# Revit family: colum
name_source: partatom
category: Tragwerksstützen
revit_build: Autodesk Revit 2018 (Build: 20190510_1515(x64)
units: mm (PartAtom-declared; Revit-internal decimal feet)

## family parameters
Beim Laden mit Abzugskörper schneiden = Nein
Gemeinsam genutzt = Nein
Immer als Geometrie exportieren = Nein
In verdeckten Ansichten anzeigen = Von anderen Elementen verdeckte Kanten
Material für Modellverhalten = Fertigbeton
Querschnittsform = Nicht definiert
Schnittebene der Familie für Draufsichten verwenden = Ja
Trägerkürzung in Plan = Nach Begrenzungsrahmen

## types (5) — shared parameters
Kopfhoehe = 300 mm

## per-type parameters (varying)
| type | Durchmesser | KB_ | KT_ | Kopfbreite | Kopftiefe | Radius |
| D=20 | 200 mm  [stored 0.656168 ft] | 100 mm  [stored 0.328084 ft] | 100 mm  [stored 0.328084 ft] | 200 mm  [stored 0.656168 ft] | 200 mm  [stored 0.656168 ft] | 100 mm  [stored 0.328084 ft] |
| D=50 | 500 mm | 250 mm | 250 mm | 500 mm | 500 mm | 250 mm |
| D=40 | 400 mm  [stored 1.31234 ft] | 200 mm  [stored 0.656168 ft] | 200 mm  [stored 0.656168 ft] | 400 mm  [stored 1.31234 ft] | 400 mm  [stored 1.31234 ft] | 200 mm  [stored 0.656168 ft] |
| D=60 | 600 mm | 300 mm | 300 mm | 600 mm | 600 mm | 300 mm |
| D=70 | 700 mm | 350 mm | 350 mm | 700 mm | 700 mm | 350 mm |

note: [stored X ft] marks values corroborated as IEEE doubles in the binary element streams (Revit-internal decimal feet)

## geometry (parser evidence)
native form markers: Blend x2
no freeform markers — native parametric forms only
